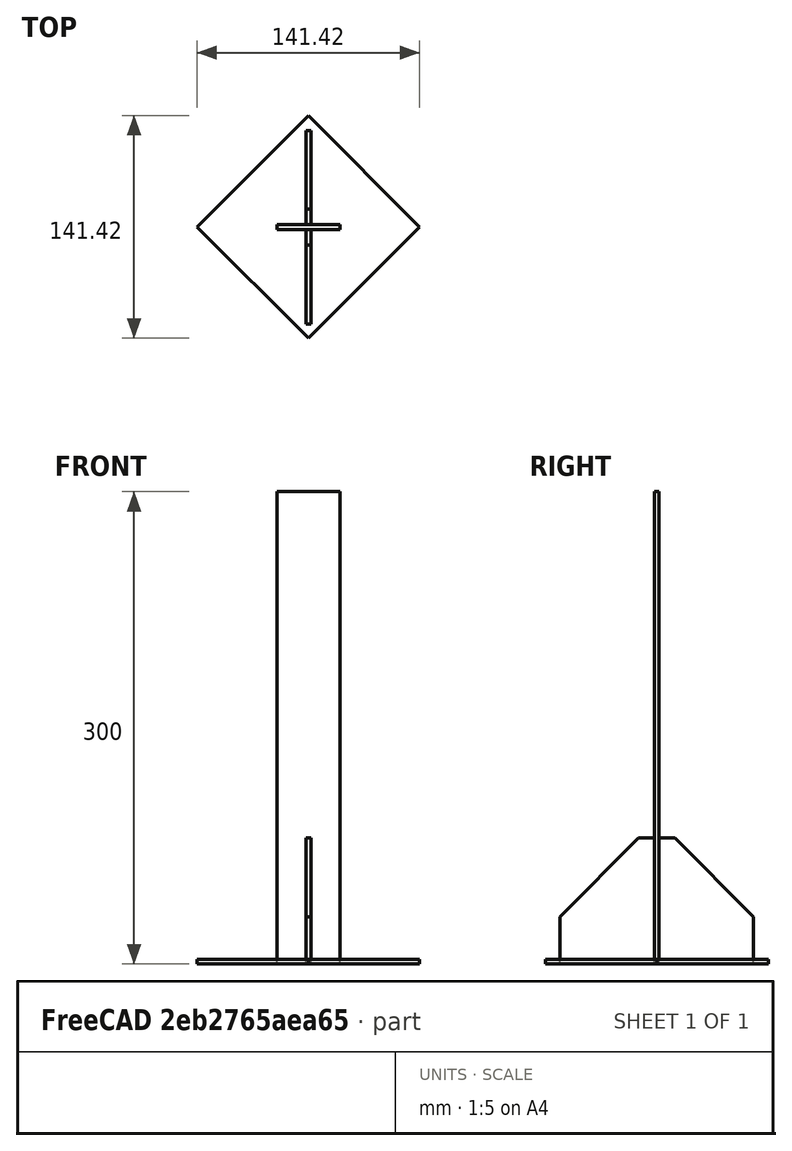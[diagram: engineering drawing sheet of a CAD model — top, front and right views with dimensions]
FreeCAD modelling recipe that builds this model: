
FCSTD DOCUMENT  (FreeCAD 0.15R4671 (Git))
Label: PeanaSensorTracker
License: All rights reserved
LicenseURL: http://en.wikipedia.org/wiki/All_rights_reserved
objects: Part::Box×4, PartDesign::Chamfer×2
note: 6 computed .brp shape members not serialized (recipe doc carries the construction recipe); baked Part::Feature solids carry a one-line shape summary decoded from their .brp

FEATURE [Part::Box] Box001  label="Base"
  Height = 3
  Length = 100
  Placement = pos=(0,0,0) rot=(0,0,1;0.785398rad)
  Width = 100
FEATURE [Part::Box] Box002  label="Columna"
  Height = 300
  Length = 40
  Placement = pos=(-20,69,0) rot=(0,0,1;0rad)
  Width = 3
FEATURE [Part::Box] Box  label="Apoyo1"
  Height = 80
  Length = 60
  Placement = pos=(1.5,72,0) rot=(0,0,1;1.5708rad)
  Width = 3
FEATURE [Part::Box] Box003  label="Apoyo002"
  Height = 80
  Length = 60
  Placement = pos=(1.5,9,0) rot=(0,0,1;1.5708rad)
  Width = 3
FEATURE [PartDesign::Chamfer] Chamfer
  Base = -> Box003 [Edge2]
  Placement = pos=(1.5,9,0) rot=(0,0,1;1.5708rad)
  Size = 50
FEATURE [PartDesign::Chamfer] Chamfer001
  Base = -> Box [Edge6]
  Placement = pos=(1.5,72,0) rot=(0,0,1;1.5708rad)
  Size = 50
